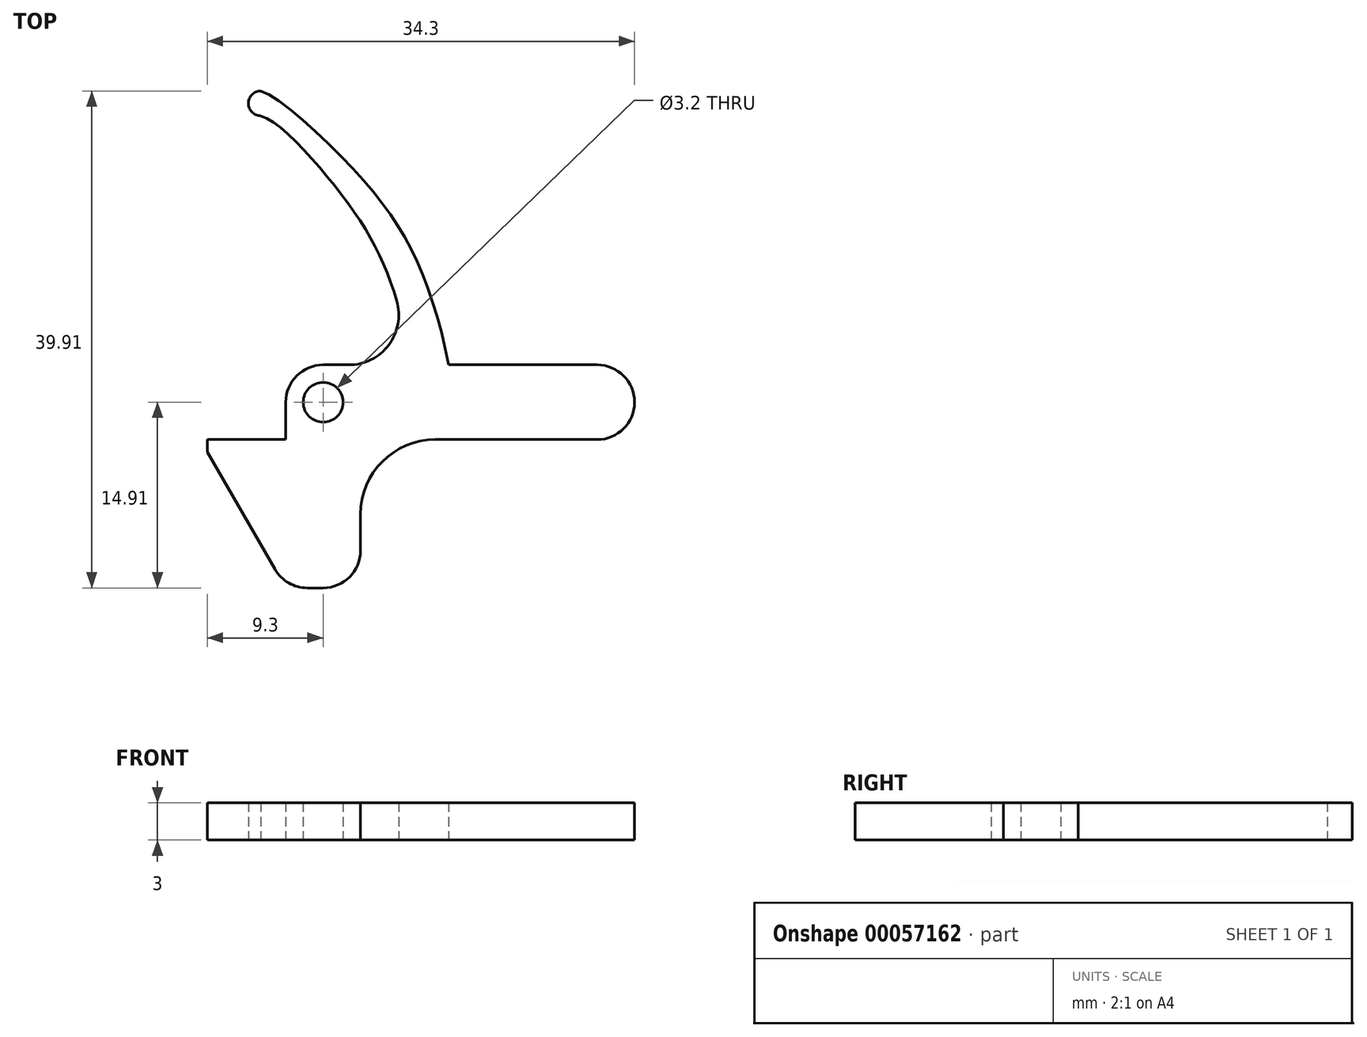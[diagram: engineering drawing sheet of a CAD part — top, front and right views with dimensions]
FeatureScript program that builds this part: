
annotation { "Feature Type Name" : "Feature", "Feature Type Description" : "" }
export const myFeature = defineFeature(function(context is Context, id is Id, definition is map)
    precondition{}
    {
        {
            var Q0;
            Q0=qCreatedBy(makeId("Top.planeOp"),FACE);
            var sketch = newSketch(context, id + "F0", { "sketchPlane" : qUnion([Q0])});
            skCircle(sketch, "E0", {"center": v(0, 0) * mm, "radius": 1.6 * mm});
            skCircle(sketch, "E1", {"center": v(0, 0) * mm, "radius": 3 * mm, "construction": true});
            skLineSegment(sketch, "E2", {"start": v(-3, 0) * mm, "end": v(-3, -4) * mm});
            skLineSegment(sketch, "E3", {"start": v(-3, -4) * mm, "end": v(-9.3, -4) * mm});
            skLineSegment(sketch, "E4", {"start": v(-9.3, -4) * mm, "end": v(-3, -14.91) * mm});
            skLineSegment(sketch, "E5", {"start": v(-3, -14.91) * mm, "end": v(3, -14.91) * mm});
            skLineSegment(sketch, "E6", {"start": v(0, 3) * mm, "end": v(25, 3) * mm});
            skArc(sketch, "E7", {"start": v(-3, 0) * mm, "mid": v(-2.12, 2.12) * mm, "end": v(0, 3) * mm});
            skLineSegment(sketch, "E8", {"start": v(-3, -4) * mm, "end": v(-3, -14.91) * mm, "construction": true});
            skLineSegment(sketch, "E9", {"start": v(3, -14.91) * mm, "end": v(3, -3) * mm});
            skLineSegment(sketch, "E10", {"start": v(25, 3) * mm, "end": v(25, -3) * mm});
            skLineSegment(sketch, "E11", {"start": v(25, -3) * mm, "end": v(3, -3) * mm});
            skLineSegment(sketch, "E12.bottom", {"start": v(-9.3, -4) * mm, "end": v(-3, -4) * mm});
            skLineSegment(sketch, "E12.top", {"start": v(-9.3, -3) * mm, "end": v(-3, -3) * mm});
            skLineSegment(sketch, "E12.left", {"start": v(-9.3, -4) * mm, "end": v(-9.3, -3) * mm});
            skLineSegment(sketch, "E12.right", {"start": v(-3, -4) * mm, "end": v(-3, -3) * mm});
            skFitSpline(sketch, "E13", {"points": [v(10.08, 3) * mm, v(7.1, 12.2) * mm, v(2.18, 19) * mm, v(-5, 25) * mm], "startDerivative": vector(-6.13, 31.94) * mm, "endDerivative": vector(-12.85, 4.1) * mm});
            skFitSpline(sketch, "E14", {"points": [v(7.08, 3) * mm, v(4.77, 11.3) * mm, v(0.48, 17.94) * mm, v(-5, 23) * mm], "startDerivative": vector(-5.58, 29.53) * mm, "endDerivative": vector(-12.64, 3.48) * mm});
            skArc(sketch, "E15", {"start": v(-5, 25) * mm, "mid": v(-6, 24) * mm, "end": v(-5, 23) * mm});
            skSolve(sketch);
        }
        {
            var Q0;
            Q0=qSketchRegion(id+"F0",true);
            extrude(context, id + "F1", {"entities" : qUnion([Q0]), "depth" : 3 * mm});
        }
        {
            var Q0;
            Q0=makeQuery(id+"F1.opExtrude","SWEPT_EDGE",EDGE,{"disambiguationData":[OSD([sQuery(id+"F0.wireOp",EDGE,"E4"),sQuery(id+"F0.wireOp",EDGE,"E5")])]});
            var Q1;
            Q1=makeQuery(id+"F1.opExtrude","SWEPT_EDGE",EDGE,{"disambiguationData":[OSD([sQuery(id+"F0.wireOp",EDGE,"E5"),sQuery(id+"F0.wireOp",EDGE,"E9")])]});
            var Q2;
            Q2=makeQuery(id+"F1.opExtrude","SWEPT_EDGE",EDGE,{"disambiguationData":[OSD([sQuery(id+"F0.wireOp",EDGE,"E10"),sQuery(id+"F0.wireOp",EDGE,"E11")])]});
            var Q3;
            Q3=makeQuery(id+"F1.opExtrude","SWEPT_EDGE",EDGE,{"disambiguationData":[OSD([sQuery(id+"F0.wireOp",EDGE,"E6"),sQuery(id+"F0.wireOp",EDGE,"E10")])]});
            var Q4;
            Q4=makeQuery(id+"F1.opExtrude","SWEPT_EDGE",EDGE,{"disambiguationData":[OSD([sQuery(id+"F0.wireOp",EDGE,"50cadb81-114b-4b49-b410-a9fb76fc186b.top"),sQuery(id+"F0.wireOp",EDGE,"50cadb81-114b-4b49-b410-a9fb76fc186b.left")])]});
            fillet(context, id + "F2", {"entities" : qUnion([Q0, Q1, Q2, Q3, Q4]), "radius" : 3 * mm, "allowEdgeOverflow" : false});
        }
        {
            var Q0;
            Q0=makeQuery(id+"F1.opExtrude","SWEPT_EDGE",EDGE,{"disambiguationData":[OSD([sQuery(id+"F0.wireOp",EDGE,"E9"),sQuery(id+"F0.wireOp",EDGE,"E11")])]});
            fillet(context, id + "F3", {"entities" : qUnion([Q0]), "radius" : 6 * mm, "tangentPropagation" : true, "allowEdgeOverflow" : false});
        }
        {
            var Q0;
            Q0=makeQuery(id+"F1.opExtrude","SWEPT_EDGE",EDGE,{"disambiguationData":[OSD([sQuery(id+"F0.wireOp",EDGE,"E6"),sQuery(id+"F0.wireOp",EDGE,"E14")])]});
            fillet(context, id + "F4", {"entities" : qUnion([Q0]), "radius" : 4 * mm, "allowEdgeOverflow" : false});
        }
    });
